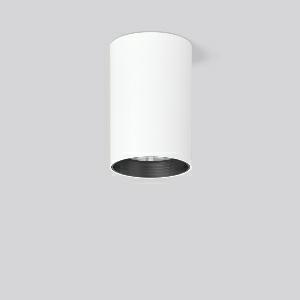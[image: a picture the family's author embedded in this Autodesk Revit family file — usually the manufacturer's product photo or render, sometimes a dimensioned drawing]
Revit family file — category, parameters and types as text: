
# Revit family: heledon_maxi_a_931229_002_1_76_02d8
name_source: partatom
category: Lighting Fixtures
units: mm (PartAtom-declared; Revit-internal decimal feet)

## family parameters
Cut with Voids When Loaded = No
Host = Face
Light Source = No
Part Type = Normal
Room Calculation Point = No
Round Connector Dimension = Use Diameter
Shared = No

## types (1)
- HELEDON maxi A (1 x LED Modul 940, 3800 lm, 4000)
    Apparent Load = 35 VA
    Approval mark = CE
    CIE Flux Codes = 96 100 100 100 100
    Color Rendering = 92
    Color Temperature = 4000
    Default Elevation = 1800 mm
    Description = Series: HELEDON maxi
Cylindrical surface-mounted downlight. Housing: die-cast aluminium, powder-coated. Internal ceiling frame polycarbonate with bayonet mounting. Black plastic ring and recessed LED to prevent glare from the side. Optical assembly with lens made of plastic (polycarbonate) for the best homogeneous light distribution - can be changed without tools. Best colour rendering index Ra>90. Suitable for Ceiling mounting. Easy installation with a separate ceiling frame with bayonet mounting and plug connection. Driver integrated. Connected via plug-in connector. High quality converter without flickering and stroboscopic effect. The following accessories can be mounted without use of tools: interchangeable lenses, decorative glasses, honeycomb louvre, clear and frosted diffusers, white interchangeable plastic ring. 
Colour: traffic white, matt (RAL 9016)
Diameter: 123 mm
Height: 183 mm
Lamp: LED
Socket: without socket
Colour temperature: 4000K
Colour rendering index (CRI): 92
System power: 35 W
Rated luminous flux: 3800 lm
Luminous efficiency: 109 lm/W
Control gear: Converter, dimmable, DALI
Protection class: I
Type of protection: IP 20
    Height = 183 mm
    Lamp = 1 x LED Modul 940
    Lamp Light Flux = 3800 lm
    Lamp count = 1
    Length = 123 mm
    Lifetime = 50000 h
    Luminous efficacy = 109 lm/W
    Manufacturer = RZB
    ModVariant = No
    Model = 931229.002.1.76
    Mounting Place = Ceiling
    Mounting Type = Surface mounted
    Number of Poles = 1
    OnlyDefault = Yes
    Power Factor = 1
    Product Name = HELEDON maxi A
    Product group = Surface mounted downlights
    ProductGroupID = 302
    Protection Class = Protection class I
    Protection Degree = IP 20
    RLX_Detail_Level = 1
    RLX_Emergency_Light_Flux = 0 lm
    RLX_Emergency_Type = 0
    RLX_Emergency_Type_DB = No
    RlxData = <blob elided: 97701 chars, md5=30e55e47>
    Socket = socket
    Standby Power = 0 W
    System Light Flux = 3800 lm
    System Power = 35 W
    Type Comments = Product without accessories
    Type Image = 931193.002.jpg
    URL = http://relux.com
    VarID = ---
    Voltage = 230 V
    Voltage Range = 220-240 V
    Weight = 0.00 kg
    Width = 0 mm  [stored 0 ft]

note: [stored X ft] marks values corroborated as IEEE doubles in the binary element streams (Revit-internal decimal feet)

## geometry (parser evidence)
native form markers: Blend x4, Sweep x12
no freeform markers — native parametric forms only
